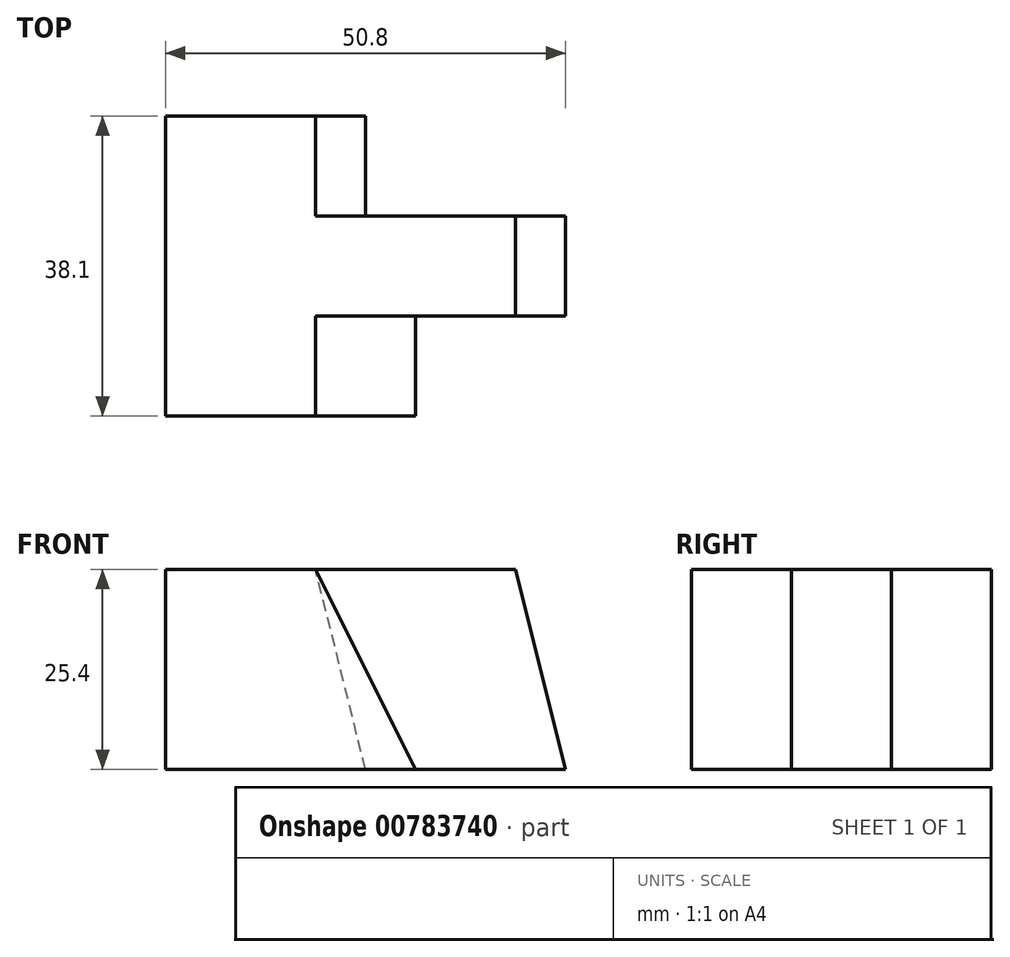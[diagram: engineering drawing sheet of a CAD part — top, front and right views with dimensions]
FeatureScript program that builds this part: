
annotation { "Feature Type Name" : "Feature", "Feature Type Description" : "" }
export const myFeature = defineFeature(function(context is Context, id is Id, definition is map)
    precondition{}
    {
        {
            var Q0;
            Q0=qCreatedBy(makeId("Front.planeOp"),FACE);
            var sketch = newSketch(context, id + "F0", { "sketchPlane" : qUnion([Q0])});
            skLineSegment(sketch, "E0", {"start": v(0, 0) * mm, "end": v(50.8, 0) * mm});
            skLineSegment(sketch, "E1", {"start": v(50.8, 0) * mm, "end": v(50.8, 25.4) * mm});
            skLineSegment(sketch, "E2", {"start": v(50.8, 25.4) * mm, "end": v(0, 25.4) * mm});
            skLineSegment(sketch, "E3", {"start": v(0, 25.4) * mm, "end": v(0, 0) * mm});
            skSolve(sketch);
        }
        {
            var Q0;
            Q0 = qSketchRegion(id + "F0", true);
            extrude(context, id + "F1", {"entities" : qUnion([Q0]), "depth" : 38.1 * mm, "offsetDistance" : 25.4 * mm});
        }
        {
            var Q0;
            Q0=makeQuery(id+"F1.opExtrude","CAP_FACE",FACE,{"disambiguationData":[OSD([sQuery(id+"F0.wireOp",EDGE,"E0"),sQuery(id+"F0.wireOp",EDGE,"E1"),sQuery(id+"F0.wireOp",EDGE,"E2"),sQuery(id+"F0.wireOp",EDGE,"E3")])],"isStart":false});
            var sketch = newSketch(context, id + "F2", { "sketchPlane" : qUnion([Q0])});
            skLineSegment(sketch, "E4", {"start": v(0, 0) * mm, "end": v(31.75, 0) * mm});
            skLineSegment(sketch, "E5", {"start": v(0, 25.4) * mm, "end": v(19.05, 25.4) * mm});
            skLineSegment(sketch, "E6", {"start": v(19.05, 25.4) * mm, "end": v(31.75, 0) * mm});
            skSolve(sketch);
        }
        {
            var Q0;
            Q0 = qSketchRegion(id + "F2", true);
            var Q1;
            {var subQ0=sQuery(id+"F2.wireOp",EDGE,"E6");Q1=makeQuery(id+"F2.imprint","IMPRINT",FACE,{"disambiguationData":[TD([[makeQuery(id+"F2.imprint","IMPRINT",EDGE,{"derivedFrom":subQ0}),1.0]])]});}
            extrude(context, id + "F3", {"entities" : qUnion([Q0, Q1]), "operationType" : NewBodyOperationType.REMOVE, "oppositeDirection" : true, "depth" : 12.7 * mm, "offsetDistance" : 25.4 * mm});
        }
        {
            var Q0;
            Q0=makeQuery(id+"F3.boolean.opBoolean","COPY",FACE,{"derivedFrom":makeQuery(id+"F3.opExtrude","CAP_FACE",FACE,{"disambiguationData":[OSD([sQuery(id+"F0.wireOp",EDGE,"E0"),sQuery(id+"F0.wireOp",EDGE,"E1"),sQuery(id+"F0.wireOp",EDGE,"E2"),sQuery(id+"F2.wireOp",EDGE,"E6")])],"isStart":false})});
            var sketch = newSketch(context, id + "F4", { "sketchPlane" : qUnion([Q0])});
            skLineSegment(sketch, "E7", {"start": v(19.05, 25.4) * mm, "end": v(44.45, 25.4) * mm});
            skLineSegment(sketch, "E8", {"start": v(44.45, 25.4) * mm, "end": v(50.8, 0) * mm});
            skSolve(sketch);
        }
        {
            var Q0;
            Q0 = qSketchRegion(id + "F4", true);
            var Q1;
            {var subQ0=sQuery(id+"F4.wireOp",EDGE,"E8");Q1=makeQuery(id+"F4.imprint","IMPRINT",FACE,{"disambiguationData":[TD([[makeQuery(id+"F4.imprint","IMPRINT",EDGE,{"derivedFrom":subQ0}),1.0]])]});}
            extrude(context, id + "F5", {"entities" : qUnion([Q0, Q1]), "operationType" : NewBodyOperationType.REMOVE, "oppositeDirection" : true, "depth" : 25.4 * mm, "offsetDistance" : 25.4 * mm});
        }
        {
            var Q0;
            Q0=makeQuery(id+"F1.opExtrude","CAP_FACE",FACE,{"disambiguationData":[OSD([sQuery(id+"F0.wireOp",EDGE,"E0"),sQuery(id+"F0.wireOp",EDGE,"E1"),sQuery(id+"F0.wireOp",EDGE,"E2"),sQuery(id+"F0.wireOp",EDGE,"E3")])],"isStart":true});
            var sketch = newSketch(context, id + "F6", { "sketchPlane" : qUnion([Q0])});
            skLineSegment(sketch, "E9", {"start": v(0, 0) * mm, "end": v(-25.4, 0) * mm});
            skLineSegment(sketch, "E10", {"start": v(0, 25.4) * mm, "end": v(-19.05, 25.4) * mm});
            skLineSegment(sketch, "E11", {"start": v(-25.4, 0) * mm, "end": v(-19.05, 25.4) * mm});
            skSolve(sketch);
        }
        {
            var Q0;
            {var subQ0=sQuery(id+"F6.wireOp",EDGE,"E11");Q0=makeQuery(id+"F6.imprint","IMPRINT",FACE,{"disambiguationData":[TD([[makeQuery(id+"F6.imprint","IMPRINT",EDGE,{"derivedFrom":subQ0}),1.0]])]});}
            extrude(context, id + "F7", {"entities" : qUnion([Q0]), "operationType" : NewBodyOperationType.REMOVE, "oppositeDirection" : true, "depth" : 12.7 * mm, "offsetDistance" : 25.4 * mm});
        }
    });
